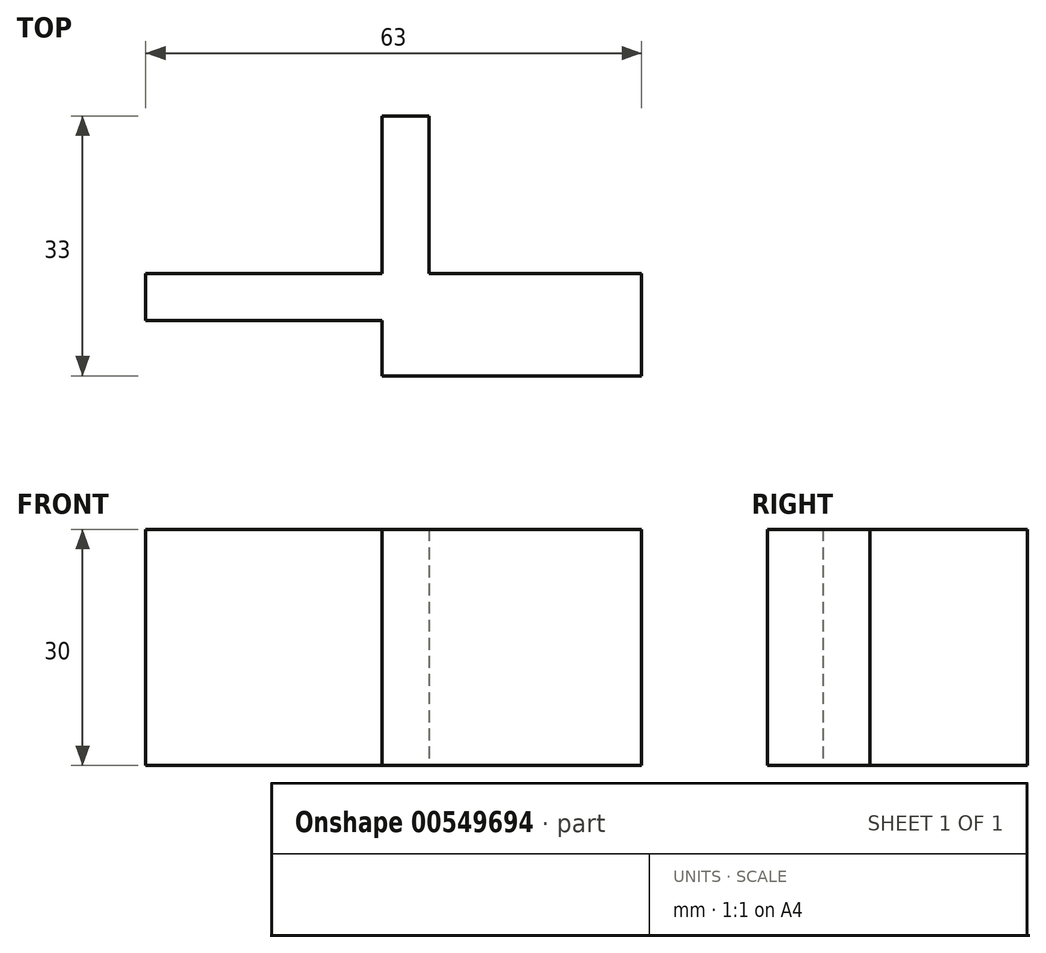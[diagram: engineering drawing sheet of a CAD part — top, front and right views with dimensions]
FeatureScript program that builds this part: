
annotation { "Feature Type Name" : "Feature", "Feature Type Description" : "" }
export const myFeature = defineFeature(function(context is Context, id is Id, definition is map)
    precondition{}
    {
        {
            var Q0;
            Q0=qCreatedBy(makeId("Top.planeOp"),FACE);
            var sketch = newSketch(context, id + "F0", { "sketchPlane" : qUnion([Q0])});
            skLineSegment(sketch, "E0", {"start": v(0, 0) * mm, "end": v(0, 13) * mm});
            skLineSegment(sketch, "E1", {"start": v(0, 13) * mm, "end": v(-27, 13) * mm});
            skLineSegment(sketch, "E2", {"start": v(-27, 13) * mm, "end": v(-27, 33) * mm});
            skLineSegment(sketch, "E3", {"start": v(-27, 33) * mm, "end": v(-33, 33) * mm});
            skLineSegment(sketch, "E4", {"start": v(-33, 33) * mm, "end": v(-33, 13) * mm});
            skLineSegment(sketch, "E5", {"start": v(-33, 13) * mm, "end": v(-63, 13) * mm});
            skLineSegment(sketch, "E6", {"start": v(-63, 13) * mm, "end": v(-63, 7) * mm});
            skLineSegment(sketch, "E7", {"start": v(-63, 7) * mm, "end": v(-33, 7) * mm});
            skLineSegment(sketch, "E8", {"start": v(-33, 7) * mm, "end": v(-33, 0) * mm});
            skLineSegment(sketch, "E9", {"start": v(-33, 0) * mm, "end": v(0, 0) * mm});
            skSolve(sketch);
        }
        {
            var Q0;
            Q0=makeQuery(id+"F0.imprint","IMPRINT",FACE,{"disambiguationData":[TD([[makeQuery(id+"F0.imprint","IMPRINT",EDGE,{"derivedFrom":sQuery(id+"F0.wireOp",EDGE,"E0")}),1.0]])]});
            extrude(context, id + "F1", {"entities" : qUnion([Q0]), "depth" : 30 * mm, "offsetDistance" : 25 * mm});
        }
    });
